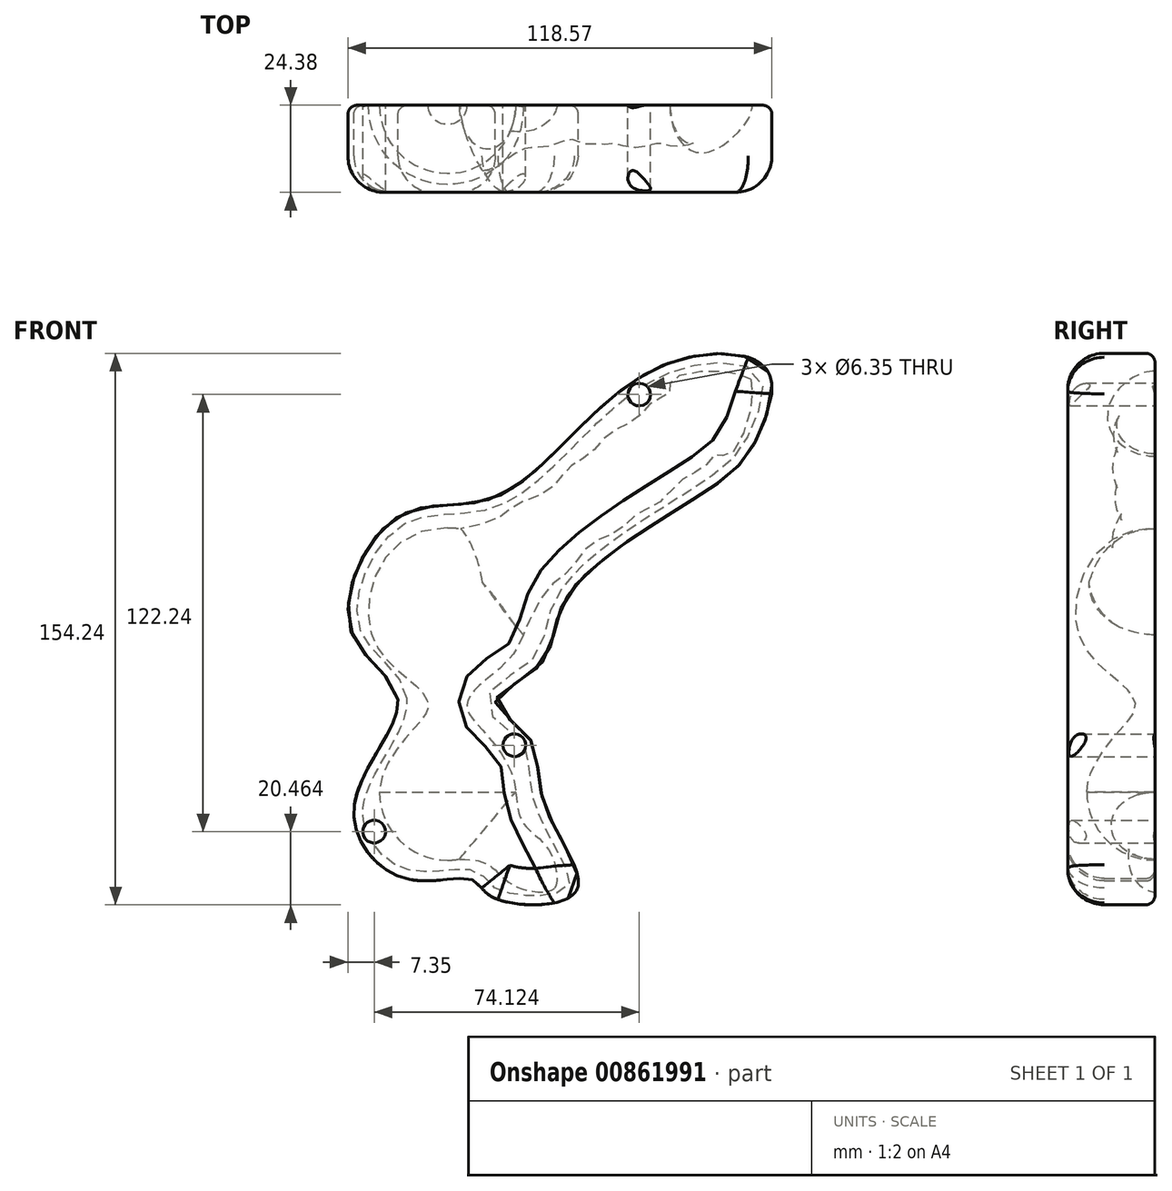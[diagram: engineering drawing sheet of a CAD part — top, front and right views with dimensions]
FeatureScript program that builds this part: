
annotation { "Feature Type Name" : "Feature", "Feature Type Description" : "" }
export const myFeature = defineFeature(function(context is Context, id is Id, definition is map)
    precondition{}
    {
        {
            var Q0;
            Q0=qCreatedBy(makeId("Front.planeOp"),FACE);
            var sketch = newSketch(context, id + "F0", { "sketchPlane" : qUnion([Q0])});
            skArc(sketch, "E0", {"start": v(0, -69.85) * mm, "mid": v(13.47, -64.27) * mm, "end": v(19.05, -50.8) * mm});
            skFitSpline(sketch, "E1", {"points": [v(-0.01, 23.13) * mm, v(21.58, -5.45) * mm, v(9.13, -20.77) * mm, v(5.4, -26.76) * mm, v(8.89, -32.47) * mm, v(19.05, -50.8) * mm], "startDerivative": vector(184.16, 1) * mm, "endDerivative": vector(2.36, -95.96) * mm});
            skLineSegment(sketch, "E2", {"start": v(0, 23.13) * mm, "end": v(0, -69.85) * mm});
            skSolve(sketch);
        }
        {
            var Q0;
            Q0=makeQuery(id+"F0.imprint","IMPRINT",FACE,{"disambiguationData":[TD([[makeQuery(id+"F0.imprint","IMPRINT",EDGE,{"derivedFrom":sQuery(id+"F0.wireOp",EDGE,"E0")}),1.0]])]});
            var Q1;
            Q1=sQuery(id+"F0.wireOp",EDGE,"E2");
            revolve(context, id + "F1", {"surfaceOperationType" : NewSurfaceOperationType.NEW, "entities" : qUnion([Q0]), "axis" : qUnion([Q1]), "revolveType" : RevolveType.FULL});
        }
        {
            var Q0;
            Q0=qCreatedBy(makeId("Front.planeOp"),FACE);
            var sketch = newSketch(context, id + "F2", { "sketchPlane" : qUnion([Q0])});
            skLineSegment(sketch, "E3", {"start": v(0, -50.6) * mm, "end": v(29.97, -77.77) * mm});
            skFitSpline(sketch, "E4", {"points": [v(19.06, -50.8) * mm, v(21.67, -60.14) * mm, v(28.3, -66.98) * mm, v(29.97, -77.77) * mm, v(0, -69.87) * mm], "startDerivative": vector(7.5, -65.65) * mm, "endDerivative": vector(-157.41, 58.8) * mm});
            skLineSegment(sketch, "E5", {"start": v(19.06, -50.8) * mm, "end": v(0, -50.6) * mm});
            skSolve(sketch);
        }
        {
            var Q0;
            Q0=makeQuery(id+"F2.imprint","IMPRINT",FACE,{"disambiguationData":[TD([[makeQuery(id+"F2.imprint","IMPRINT",EDGE,{"derivedFrom":sQuery(id+"F2.wireOp",EDGE,"E3")}),1.0]])]});
            var Q1;
            Q1=sQuery(id+"F2.wireOp",EDGE,"E3");
            revolve(context, id + "F3", {"operationType" : NewBodyOperationType.ADD, "surfaceOperationType" : NewSurfaceOperationType.NEW, "entities" : qUnion([Q0]), "axis" : qUnion([Q1]), "revolveType" : RevolveType.FULL});
        }
        {
            var Q0;
            Q0=qCreatedBy(makeId("Front.planeOp"),FACE);
            var sketch = newSketch(context, id + "F4", { "sketchPlane" : qUnion([Q0])});
            skLineSegment(sketch, "E6", {"start": v(0, 0) * mm, "end": v(84.83, 64.67) * mm});
            skFitSpline(sketch, "E7", {"points": [v(84.83, 64.67) * mm, v(84.83, 56.57) * mm, v(78.49, 43.23) * mm, v(75.2, 43.78) * mm, v(71.9, 40.23) * mm, v(65.99, 36.92) * mm, v(59.6, 30.54) * mm, v(52.75, 26.75) * mm, v(47.3, 22.02) * mm, v(39.98, 18.48) * mm, v(33.76, 10.84) * mm, v(27.55, 5.5) * mm, v(21.16, -6.9) * mm, v(0, 0) * mm], "startDerivative": vector(13.16, -101.21) * mm, "endDerivative": vector(-606.42, -29.56) * mm});
            skSolve(sketch);
        }
        {
            var Q0;
            Q0=makeQuery(id+"F4.imprint","IMPRINT",FACE,{"disambiguationData":[TD([[makeQuery(id+"F4.imprint","IMPRINT",EDGE,{"derivedFrom":sQuery(id+"F4.wireOp",EDGE,"E6")}),-1.0]])]});
            var Q1;
            Q1=sQuery(id+"F4.wireOp",EDGE,"E6");
            revolve(context, id + "F5", {"operationType" : NewBodyOperationType.ADD, "surfaceOperationType" : NewSurfaceOperationType.NEW, "entities" : qUnion([Q0]), "axis" : qUnion([Q1]), "revolveType" : RevolveType.FULL});
        }
        {
            var Q0;
            Q0=qCreatedBy(makeId("Front.planeOp"),FACE);
            var sketch = newSketch(context, id + "F6", { "sketchPlane" : qUnion([Q0])});
            skFitSpline(sketch, "E8", {"points": [v(-13.87, -24.9) * mm, v(-27.09, -5.5) * mm, v(-13.7, 26.23) * mm, v(14.1, 31.94) * mm, v(56.55, 66.82) * mm, v(89.32, 67.24) * mm, v(86.8, 48.75) * mm, v(76.19, 36.08) * mm, v(33.66, 4.19) * mm, v(26.16, -14.89) * mm, v(13.34, -25.52) * mm, v(22.72, -35.53) * mm, v(27.1, -54.29) * mm, v(35.85, -78.68) * mm, v(12.71, -80.24) * mm, v(6.77, -75.24) * mm, v(-11.99, -74.92) * mm, v(-26.06, -54.6) * mm, v(-13.87, -24.9) * mm]});
            skCircle(sketch, "E9", {"center": v(18.7, -37.69) * mm, "radius": 3.18 * mm});
            skCircle(sketch, "E10", {"center": v(-20.5, -61.87) * mm, "radius": 3.18 * mm});
            skCircle(sketch, "E11", {"center": v(53.62, 60.37) * mm, "radius": 3.18 * mm});
            skSolve(sketch);
        }
        {
            var Q0;
            Q0=makeQuery(id+"F6.imprint","IMPRINT",FACE,{"disambiguationData":[TD([[makeQuery(id+"F6.imprint","IMPRINT",EDGE,{"derivedFrom":sQuery(id+"F6.wireOp",EDGE,"E8")}),-1.0]])]});
            extrude(context, id + "F7", {"entities" : qUnion([Q0]), "depth" : 24.38 * mm, "offsetDistance" : 25.4 * mm});
        }
        {
            var Q0;
            Q0=makeQuery(id+"F6.imprint","IMPRINT",FACE,{"disambiguationData":[TD([[makeQuery(id+"F6.imprint","IMPRINT",EDGE,{"derivedFrom":sQuery(id+"F6.wireOp",EDGE,"E9")}),1.0]])]});
            var Q1;
            Q1=makeQuery(id+"F6.imprint","IMPRINT",FACE,{"disambiguationData":[TD([[makeQuery(id+"F6.imprint","IMPRINT",EDGE,{"derivedFrom":sQuery(id+"F6.wireOp",EDGE,"E10")}),1.0]])]});
            var Q2;
            Q2=makeQuery(id+"F6.imprint","IMPRINT",FACE,{"disambiguationData":[TD([[makeQuery(id+"F6.imprint","IMPRINT",EDGE,{"derivedFrom":sQuery(id+"F6.wireOp",EDGE,"E11")}),1.0]])]});
            extrude(context, id + "F8", {"entities" : qUnion([Q0, Q1, Q2]), "operationType" : NewBodyOperationType.REMOVE, "depth" : 7.62 * mm, "offsetDistance" : 25.4 * mm});
        }
        {
            var Q0;
            Q0=makeQuery(id+"F7.opExtrude","CAP_EDGE",EDGE,{"disambiguationData":[OSD([sQuery(id+"F6.wireOp",EDGE,"E8")])],"isStart":true});
            fillet(context, id + "F9", {"entities" : qUnion([Q0]), "radius" : 2.54 * mm, "tangentPropagation" : true, "allowEdgeOverflow" : false});
        }
        {
            var Q0;
            Q0=makeQuery(id+"F7.opExtrude","CAP_EDGE",EDGE,{"disambiguationData":[OSD([sQuery(id+"F6.wireOp",EDGE,"E8")])],"isStart":false});
            fillet(context, id + "F10", {"entities" : qUnion([Q0]), "radius" : 10.16 * mm, "tangentPropagation" : true, "allowEdgeOverflow" : false});
        }
        {
            var Q0;
            Q0=makeQuery(id+"F1.opRevolve","SWEPT_BODY",BODY,{"disambiguationData":[OSD([sQuery(id+"F0.wireOp",EDGE,"E0"),sQuery(id+"F0.wireOp",EDGE,"E1"),sQuery(id+"F0.wireOp",EDGE,"E2")])]});
            var Q1;
            Q1=makeQuery(id+"F7.opExtrude","SWEPT_BODY",BODY,{"disambiguationData":[OSD([sQuery(id+"F6.wireOp",EDGE,"E8"),sQuery(id+"F6.wireOp",EDGE,"E9"),sQuery(id+"F6.wireOp",EDGE,"E10"),sQuery(id+"F6.wireOp",EDGE,"E11")])]});
            booleanBodies(context, id + "F11", {"operationType" : BooleanOperationType.SUBTRACTION, "tools" : qUnion([Q0]), "targets" : qUnion([Q1])});
        }
    });
